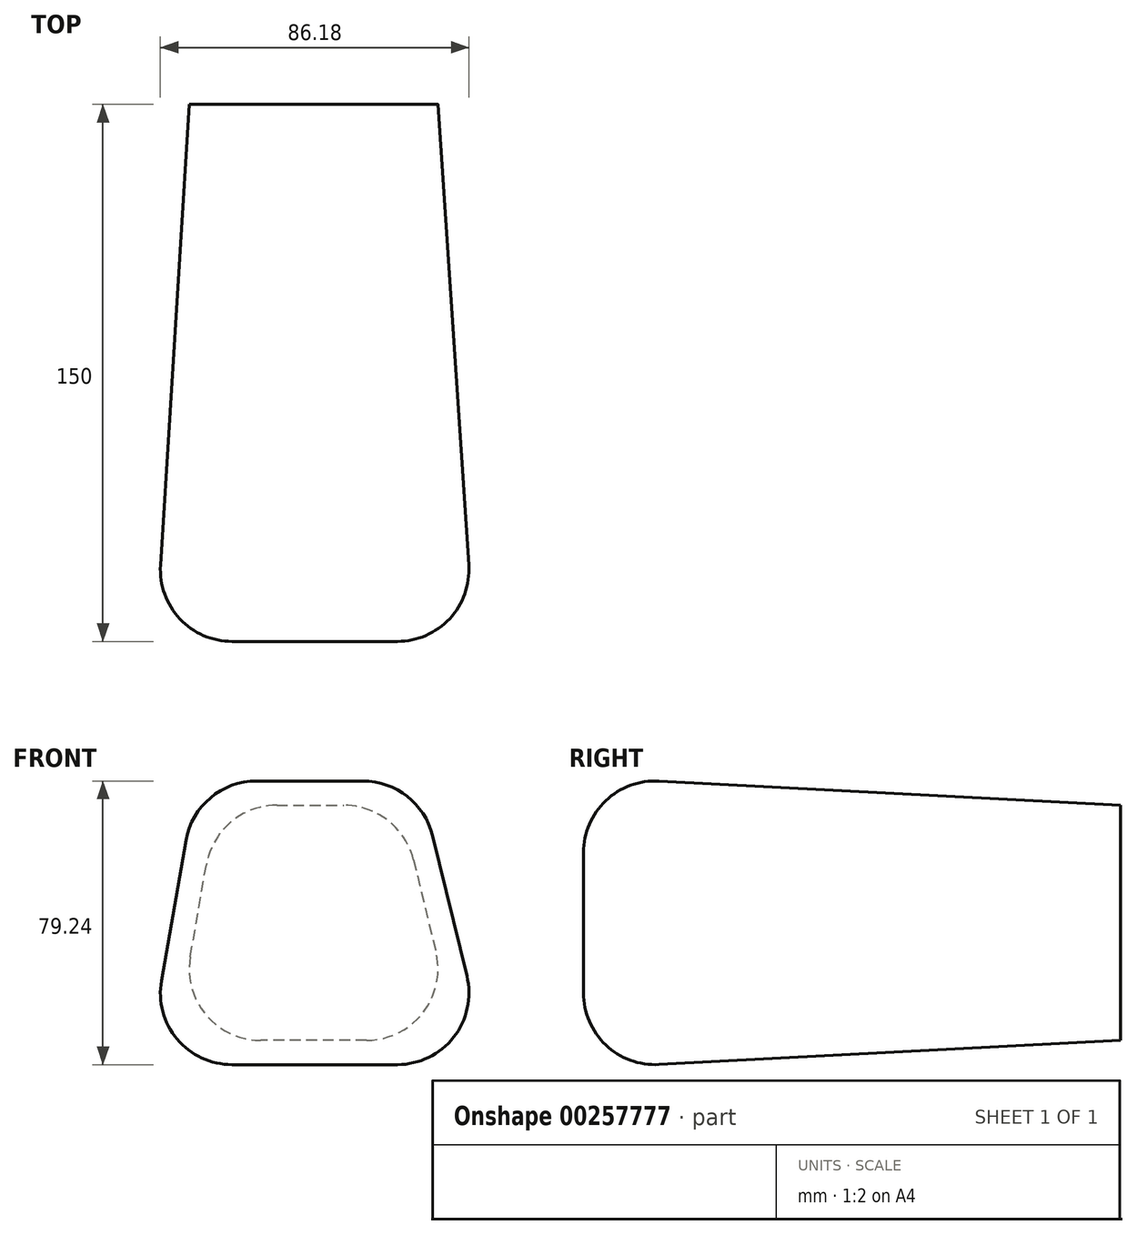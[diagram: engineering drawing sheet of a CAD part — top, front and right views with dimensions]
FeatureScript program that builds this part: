
annotation { "Feature Type Name" : "Feature", "Feature Type Description" : "" }
export const myFeature = defineFeature(function(context is Context, id is Id, definition is map)
    precondition{}
    {
        {
            var Q0;
            Q0=qCreatedBy(makeId("Front.planeOp"),FACE);
            var sketch = newSketch(context, id + "F0", { "sketchPlane" : qUnion([Q0])});
            skLineSegment(sketch, "E0", {"start": v(-52.8, -13.66) * mm, "end": v(-41.33, 52) * mm});
            skLineSegment(sketch, "E1", {"start": v(-41.33, 52) * mm, "end": v(9.87, 52) * mm});
            skLineSegment(sketch, "E2", {"start": v(9.87, 52) * mm, "end": v(25.94, -13.66) * mm});
            skLineSegment(sketch, "E3", {"start": v(-52.8, -13.66) * mm, "end": v(25.94, -13.66) * mm});
            skSolve(sketch);
        }
        {
            var Q0;
            Q0=makeQuery(id+"F0.imprint","IMPRINT",FACE,{"disambiguationData":[TD([[makeQuery(id+"F0.imprint","IMPRINT",EDGE,{"derivedFrom":sQuery(id+"F0.wireOp",EDGE,"E0")}),-1.0]])]});
            extrude(context, id + "F1", {"entities" : qUnion([Q0]), "depth" : 150 * mm, "hasDraft" : true, "draftAngle" : 3 * degree});
        }
        {
            var Q0;
            Q0=makeQuery(id+"F1.opExtrude","SWEPT_EDGE",EDGE,{"disambiguationData":[OSD([sQuery(id+"F0.wireOp",EDGE,"E0"),sQuery(id+"F0.wireOp",EDGE,"E1")])]});
            var Q1;
            Q1=makeQuery(id+"F1.opExtrude","SWEPT_EDGE",EDGE,{"disambiguationData":[OSD([sQuery(id+"F0.wireOp",EDGE,"E1"),sQuery(id+"F0.wireOp",EDGE,"E2")])]});
            var Q2;
            Q2=makeQuery(id+"F1.opExtrude","SWEPT_EDGE",EDGE,{"disambiguationData":[OSD([sQuery(id+"F0.wireOp",EDGE,"E2"),sQuery(id+"F0.wireOp",EDGE,"E3")])]});
            var Q3;
            Q3=makeQuery(id+"F1.opExtrude","SWEPT_EDGE",EDGE,{"disambiguationData":[OSD([sQuery(id+"F0.wireOp",EDGE,"E0"),sQuery(id+"F0.wireOp",EDGE,"E3")])]});
            var Q4;
            Q4=makeQuery(id+"F1.opExtrude","CAP_EDGE",EDGE,{"disambiguationData":[OSD([sQuery(id+"F0.wireOp",EDGE,"E3")])],"isStart":false});
            var Q5;
            Q5=makeQuery(id+"F1.opExtrude","CAP_EDGE",EDGE,{"disambiguationData":[OSD([sQuery(id+"F0.wireOp",EDGE,"E1")])],"isStart":false});
            var Q6;
            Q6=makeQuery(id+"F1.opExtrude","CAP_EDGE",EDGE,{"disambiguationData":[OSD([sQuery(id+"F0.wireOp",EDGE,"E0")])],"isStart":false});
            var Q7;
            Q7=makeQuery(id+"F1.opExtrude","CAP_EDGE",EDGE,{"disambiguationData":[OSD([sQuery(id+"F0.wireOp",EDGE,"E2")])],"isStart":false});
            var Q8;
            Q8=makeQuery(id+"F1.opExtrude","CAP_FACE",FACE,{"disambiguationData":[OSD([sQuery(id+"F0.wireOp",EDGE,"E0"),sQuery(id+"F0.wireOp",EDGE,"E1"),sQuery(id+"F0.wireOp",EDGE,"E2"),sQuery(id+"F0.wireOp",EDGE,"E3")])],"isStart":false});
            fillet(context, id + "F2", {"entities" : qUnion([Q0, Q1, Q2, Q3, Q4, Q5, Q6, Q7, Q8]), "radius" : 20 * mm, "tangentPropagation" : true, "allowEdgeOverflow" : false});
        }
    });
